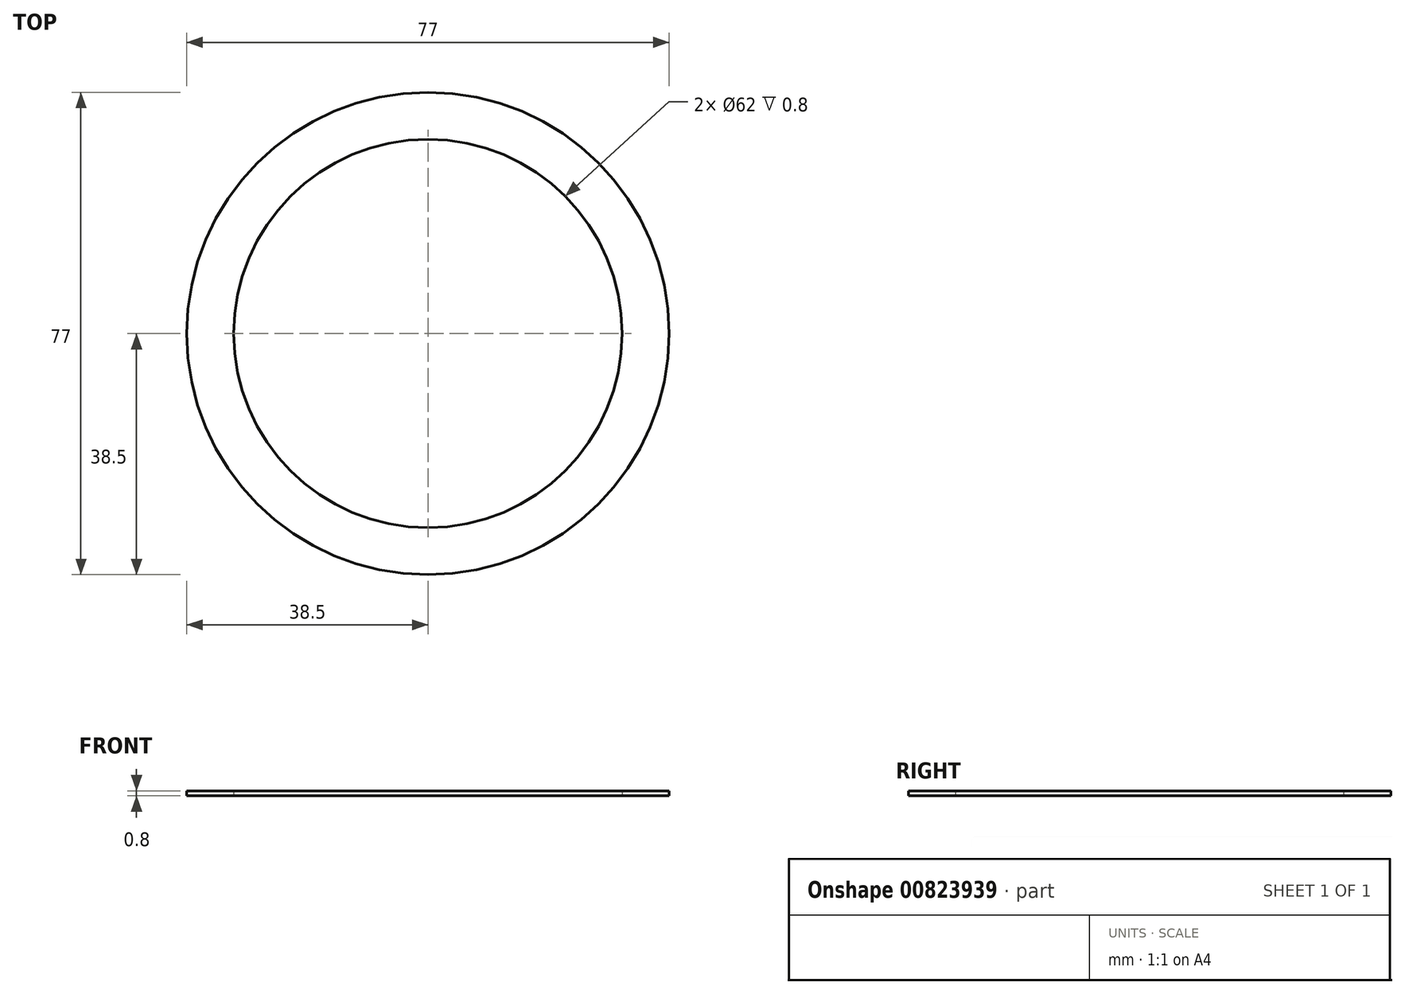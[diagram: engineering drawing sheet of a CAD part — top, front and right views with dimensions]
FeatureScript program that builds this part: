
annotation { "Feature Type Name" : "Feature", "Feature Type Description" : "" }
export const myFeature = defineFeature(function(context is Context, id is Id, definition is map)
    precondition{}
    {
        {
            var Q0;
            Q0=qCreatedBy(makeId("Top.planeOp"),FACE);
            var sketch = newSketch(context, id + "F0", { "sketchPlane" : qUnion([Q0])});
            skCircle(sketch, "E0", {"center": v(0, 0) * mm, "radius": 38.5 * mm});
            skCircle(sketch, "E1", {"center": v(0, 0) * mm, "radius": 31 * mm});
            skSolve(sketch);
        }
        {
            var Q0;
            Q0=qSketchRegion(id+"F0",true);
            extrude(context, id + "F1", {"entities" : qUnion([Q0]), "depth" : 0.8 * mm, "offsetDistance" : 25 * mm});
        }
    });
